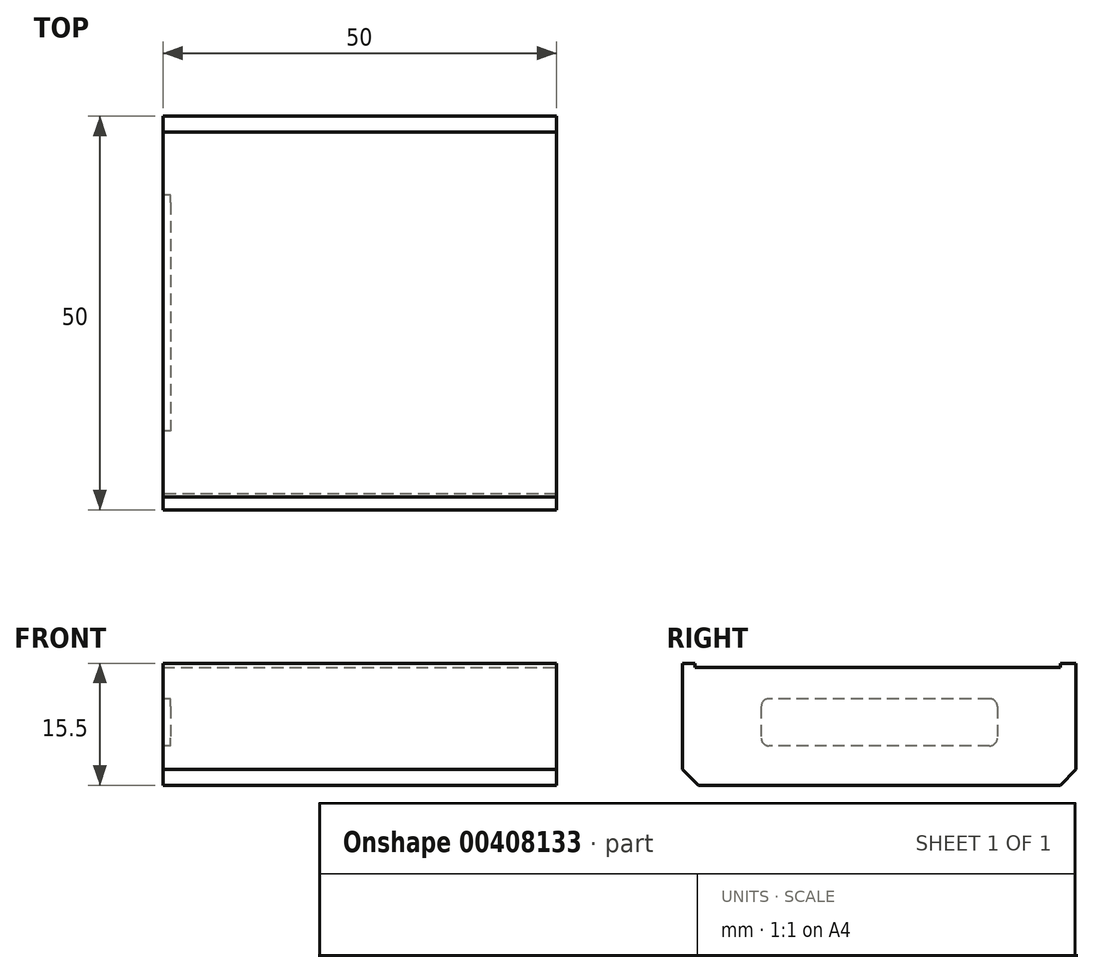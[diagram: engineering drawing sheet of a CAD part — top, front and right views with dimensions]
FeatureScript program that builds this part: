
annotation { "Feature Type Name" : "Feature", "Feature Type Description" : "" }
export const myFeature = defineFeature(function(context is Context, id is Id, definition is map)
    precondition{}
    {
        {
            var Q0;
            Q0=qCreatedBy(makeId("Top.planeOp"),FACE);
            var sketch = newSketch(context, id + "F0", { "sketchPlane" : qUnion([Q0])});
            skLineSegment(sketch, "E0.bottom", {"start": v(0, 0) * mm, "end": v(50, 0) * mm});
            skLineSegment(sketch, "E0.top", {"start": v(0, 50) * mm, "end": v(50, 50) * mm});
            skLineSegment(sketch, "E0.left", {"start": v(0, 0) * mm, "end": v(0, 50) * mm});
            skLineSegment(sketch, "E0.right", {"start": v(50, 0) * mm, "end": v(50, 50) * mm});
            skSolve(sketch);
        }
        {
            var Q0;
            Q0=makeQuery(id+"F0.imprint","IMPRINT",FACE,{"disambiguationData":[TD([[makeQuery(id+"F0.imprint","IMPRINT",EDGE,{"derivedFrom":sQuery(id+"F0.wireOp",EDGE,"E0.bottom")}),1.0]])]});
            extrude(context, id + "F1", {"entities" : qUnion([Q0]), "depth" : 15 * mm});
        }
        {
            var Q0;
            Q0=makeQuery(id+"F1.opExtrude","CAP_EDGE",EDGE,{"disambiguationData":[OSD([sQuery(id+"F0.wireOp",EDGE,"E0.bottom")])],"isStart":true});
            var Q1;
            Q1=makeQuery(id+"F1.opExtrude","CAP_EDGE",EDGE,{"disambiguationData":[OSD([sQuery(id+"F0.wireOp",EDGE,"E0.top")])],"isStart":true});
            chamfer(context, id + "F2", {"entities" : qUnion([Q0, Q1]), "width" : 2 * mm, "tangentPropagation" : true});
        }
        {
            var Q0;
            Q0=makeQuery(id+"F1.opExtrude","SWEPT_FACE",FACE,{"disambiguationData":[OSD([sQuery(id+"F0.wireOp",EDGE,"E0.left")])]});
            var sketch = newSketch(context, id + "F3", { "sketchPlane" : qUnion([Q0])});
            skLineSegment(sketch, "E1.bottom", {"start": v(-40, 11) * mm, "end": v(-10, 11) * mm});
            skLineSegment(sketch, "E1.top", {"start": v(-40, 5.01) * mm, "end": v(-10, 5.01) * mm});
            skLineSegment(sketch, "E1.left", {"start": v(-40, 11) * mm, "end": v(-40, 5.01) * mm});
            skLineSegment(sketch, "E1.right", {"start": v(-10, 11) * mm, "end": v(-10, 5.01) * mm});
            skSolve(sketch);
        }
        {
            var Q0;
            Q0 = qSketchRegion(id + "F3", true);
            extrude(context, id + "F4", {"entities" : qUnion([Q0]), "operationType" : NewBodyOperationType.REMOVE, "oppositeDirection" : true, "depth" : 1 * mm});
        }
        {
            var Q0;
            Q0=makeQuery(id+"F4.boolean.opBoolean","COPY",EDGE,{"derivedFrom":makeQuery(id+"F4.opExtrude","SWEPT_EDGE",EDGE,{"disambiguationData":[OSD([sQuery(id+"F3.wireOp",EDGE,"E1.bottom"),sQuery(id+"F3.wireOp",EDGE,"E1.left")])]})});
            var Q1;
            Q1=makeQuery(id+"F4.boolean.opBoolean","COPY",EDGE,{"derivedFrom":makeQuery(id+"F4.opExtrude","SWEPT_EDGE",EDGE,{"disambiguationData":[OSD([sQuery(id+"F3.wireOp",EDGE,"E1.top"),sQuery(id+"F3.wireOp",EDGE,"E1.left")])]})});
            var Q2;
            Q2=makeQuery(id+"F4.boolean.opBoolean","COPY",EDGE,{"derivedFrom":makeQuery(id+"F4.opExtrude","SWEPT_EDGE",EDGE,{"disambiguationData":[OSD([sQuery(id+"F3.wireOp",EDGE,"E1.bottom"),sQuery(id+"F3.wireOp",EDGE,"E1.right")])]})});
            var Q3;
            Q3=makeQuery(id+"F4.boolean.opBoolean","COPY",EDGE,{"derivedFrom":makeQuery(id+"F4.opExtrude","SWEPT_EDGE",EDGE,{"disambiguationData":[OSD([sQuery(id+"F3.wireOp",EDGE,"E1.top"),sQuery(id+"F3.wireOp",EDGE,"E1.right")])]})});
            fillet(context, id + "F5", {"entities" : qUnion([Q0, Q1, Q2, Q3]), "radius" : 1 * mm, "tangentPropagation" : true, "allowEdgeOverflow" : false});
        }
        {
            var Q0;
            Q0=makeQuery(id+"F1.opExtrude","CAP_FACE",FACE,{"disambiguationData":[OSD([sQuery(id+"F0.wireOp",EDGE,"E0.bottom"),sQuery(id+"F0.wireOp",EDGE,"E0.top"),sQuery(id+"F0.wireOp",EDGE,"E0.left"),sQuery(id+"F0.wireOp",EDGE,"E0.right")])],"isStart":false});
            var sketch = newSketch(context, id + "F6", { "sketchPlane" : qUnion([Q0])});
            skLineSegment(sketch, "E2.bottom", {"start": v(0, 50) * mm, "end": v(50, 50) * mm});
            skLineSegment(sketch, "E2.top", {"start": v(0, 48) * mm, "end": v(50, 48) * mm});
            skLineSegment(sketch, "E2.left", {"start": v(0, 50) * mm, "end": v(0, 48) * mm});
            skLineSegment(sketch, "E2.right", {"start": v(50, 50) * mm, "end": v(50, 48) * mm});
            skLineSegment(sketch, "E3.bottom", {"start": v(0, 0) * mm, "end": v(50, 0) * mm});
            skLineSegment(sketch, "E3.top", {"start": v(0, 1.6) * mm, "end": v(50, 1.6) * mm});
            skLineSegment(sketch, "E3.left", {"start": v(0, 0) * mm, "end": v(0, 1.6) * mm});
            skLineSegment(sketch, "E3.right", {"start": v(50, 0) * mm, "end": v(50, 1.6) * mm});
            skSolve(sketch);
        }
        {
            var Q0;
            Q0=makeQuery(id+"F6.imprint","IMPRINT",FACE,{"disambiguationData":[TD([[makeQuery(id+"F6.imprint","IMPRINT",EDGE,{"derivedFrom":sQuery(id+"F6.wireOp",EDGE,"E2.bottom")}),-1.0]])]});
            var Q1;
            Q1=makeQuery(id+"F6.imprint","IMPRINT",FACE,{"disambiguationData":[TD([[makeQuery(id+"F6.imprint","IMPRINT",EDGE,{"derivedFrom":sQuery(id+"F6.wireOp",EDGE,"E3.bottom")}),1.0]])]});
            extrude(context, id + "F7", {"entities" : qUnion([Q0, Q1]), "operationType" : NewBodyOperationType.ADD, "depth" : 0.5 * mm});
        }
    });
